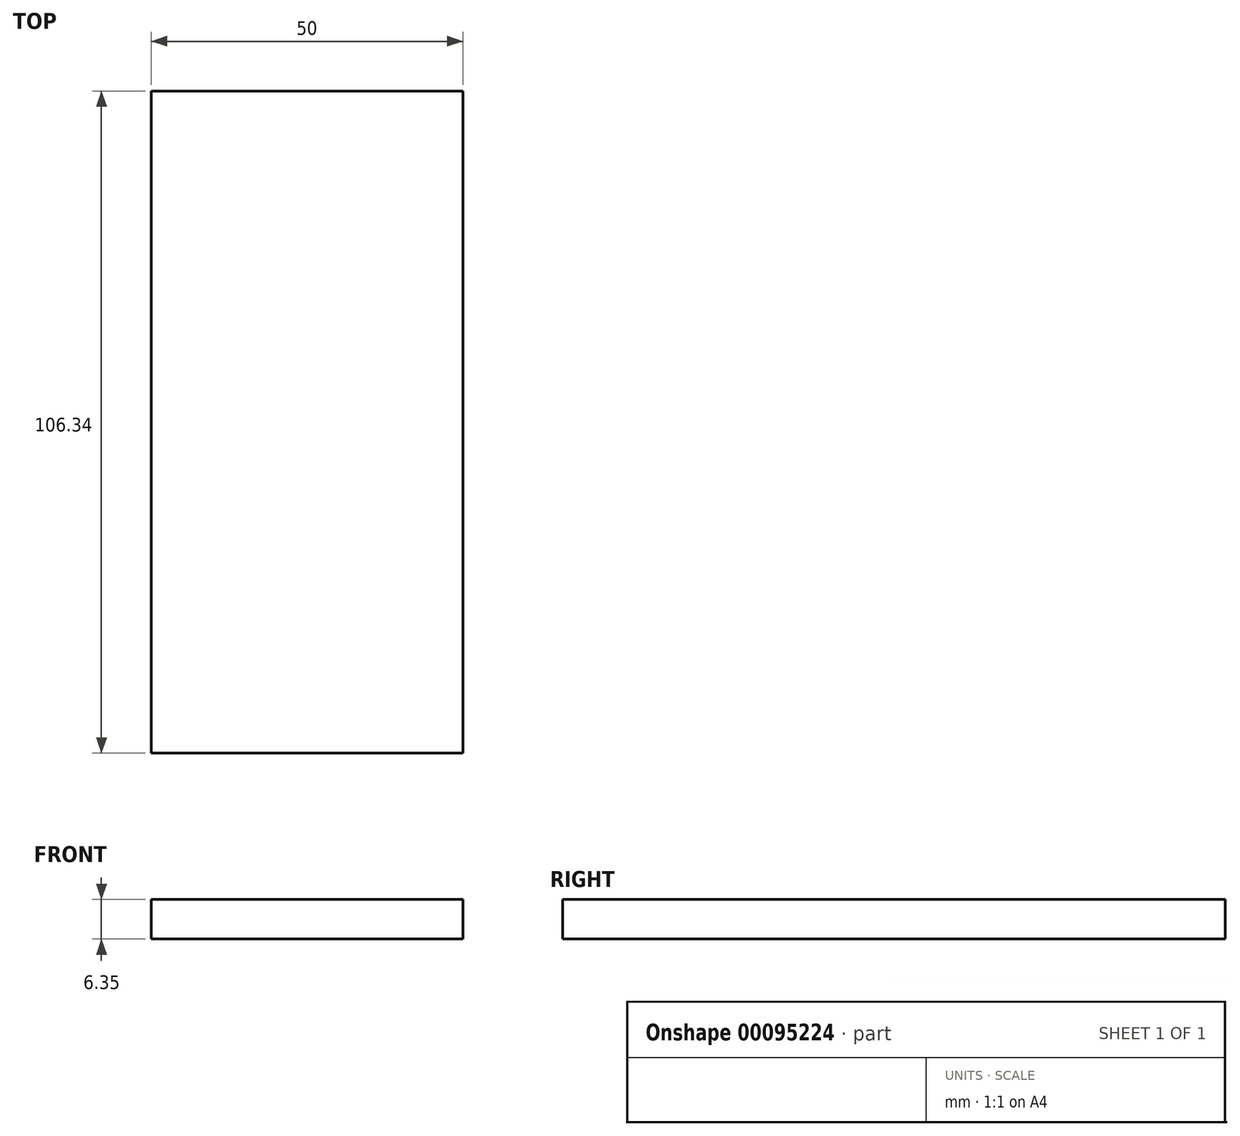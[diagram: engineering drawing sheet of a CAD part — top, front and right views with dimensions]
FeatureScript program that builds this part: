
annotation { "Feature Type Name" : "Feature", "Feature Type Description" : "" }
export const myFeature = defineFeature(function(context is Context, id is Id, definition is map)
    precondition{}
    {
        {
            var Q0;
            Q0=qCreatedBy(makeId("Top.planeOp"),FACE);
            var sketch = newSketch(context, id + "F0", { "sketchPlane" : qUnion([Q0])});
            skLineSegment(sketch, "E0.bottom", {"start": v(25, 53.17) * mm, "end": v(-25, 53.17) * mm});
            skLineSegment(sketch, "E0.top", {"start": v(25, -53.17) * mm, "end": v(-25, -53.17) * mm});
            skLineSegment(sketch, "E0.left", {"start": v(25, 53.17) * mm, "end": v(25, -53.17) * mm});
            skLineSegment(sketch, "E0.right", {"start": v(-25, 53.17) * mm, "end": v(-25, -53.17) * mm});
            skPoint(sketch, "E0.middle", {"position": v(0, 0) * mm});
            skSolve(sketch);
        }
        {
            var Q0;
            Q0=makeQuery(id+"F0.imprint","IMPRINT",FACE,{"disambiguationData":[TD([[makeQuery(id+"F0.imprint","IMPRINT",EDGE,{"derivedFrom":sQuery(id+"F0.wireOp",EDGE,"E0.bottom")}),1.0]])]});
            extrude(context, id + "F1", {"entities" : qUnion([Q0]), "depth" : 6.35 * mm});
        }
    });
